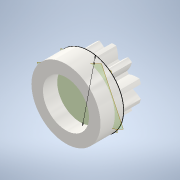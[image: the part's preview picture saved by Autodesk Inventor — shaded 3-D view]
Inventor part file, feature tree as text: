
AUTODESK INVENTOR PART (.ipt)
format: ipt  version: 2022 (Build 260153070, 153G)  size: 355,840 bytes
history: native  units: mm (DEFAULTED — no unit token found)
features: sketch x7, other x6, extrude x5, plane x5
ambient origin geometry x8: Origin, YZ Plane, XZ Plane, XY Plane, X Axis, Y Axis, Z Axis, Center Point
bodies: Solid1 (feature_tree)
feature tree (23):
  extrude  "Extrusion1"  Depth=3.0mm TaperAngle=0.0deg
  plane  "Work Plane2"
  plane  "Work Plane8"
  plane  "Work Plane9"
  other  "Spur Gear"
  plane  "Work Plane12"
  plane  "Work Plane14"
  extrude  "Extrusion4"  Depth=10.0mm TaperAngle=0.0deg
  extrude  "Extrusion3"  Depth=3.141593mm TaperAngle=0.0deg
  extrude  "Extrusion5"  TaperAngle=0.0deg  [1 undecoded]
  extrude  "Extrusion6"  Depth=21.0mm
  sketch  "Sketch9"  dims[d53=6.0mm d54=20.0mm d55=0.0mm d60=9.0mm d61=3.0mm d62=0.0mm d63=3.0mm d64=0.0mm d65=2.0mm d66=3.0mm d67=0.0mm]
  sketch  "Sketch1"  dims[d0=7.2mm d1=3.0mm d2=0.0mm]
  sketch  "Sketch2"  dims[d3=6.0mm d4=10.0mm d5=0.0mm]
  other  "Srf1"
  sketch  "Sketch5"  dims[d16=21.0mm d17=0.0mm d34=3.141593mm]
  sketch  "Sketch6"  dims[d39=0.0mm d41=0.0mm]
  sketch  "Sketch7"  dims[d43=21.0mm d46=21.0mm]
  sketch  "Sketch8"  dims[d47=0.0mm d48=0.0mm]
  other  "Pitch Diameter"
  other  "<userpath> laptop\Desktop\SumoBot\sumobotLIDAR\sumobotLIDAR.iam"
  other  "sumobotLIDAR.iam"
  other  "Magnet:1"
note: 1 required parameter value undecoded (feature->parameter linkage not recoverable at this tier; creation-order binding heuristic only, values carry confidence <= 0.55)
